# Revit family: Window_Shade-Draper_Inc.-Colossal_Flex_Shade
name_source: partatom
category: Specialty Equipment
units: mm (PartAtom-declared; Revit-internal decimal feet)

## family parameters
Classification Number = 23.30.20.11
Cut with Voids When Loaded = No
Enable Cutting in Views = No
Host = Face
Maintain Annotation Orientation = No
Part Type = Normal
Room Calculation Point = No
Round Connector Dimension = Use Diameter
Shared = No

## types (1)
- Colossal Flex Shade - 8'
    Apparent Load = 132 VA
    C Height = 7' - 0"
    C Length = 8' - 0"
    Case Material = Paint - Draper - White
    Default Elevation = 7' - 0"
    Description = Window Shade
    Frequency = 60 Hz
    Length = 8' - 0"
    Manufacturer = Draper Inc.
    Model = Colossal FlexShade
    Notes = Maximum size 28’-9” wide x 36’ height. Other sizes available. Contact Draper for details.
    Number of Poles = 1
    Overall Height = 7' - 0"
    Phase = 1
    Power Factor = 1
    Product Documentation Link = http://www.draperinc.com
    Product Page URL = http://www.draperinc.com
    Shade Material = Fabric - Draper - SunBloc - Series SB900
    Support One = Yes
    Support Three = No
    Support Two = No
    URL = http://www.draperinc.com
    Voltage = 120 V
    Width = 1' - 0"

## geometry (parser evidence)
native form markers: Blend x7, Sweep x7
no freeform markers — native parametric forms only
